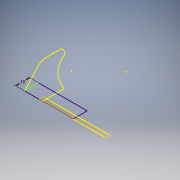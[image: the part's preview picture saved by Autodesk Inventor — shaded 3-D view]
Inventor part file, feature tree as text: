
AUTODESK INVENTOR PART (.ipt)
format: ipt  version: 2016 (Build 200138000, 138)  size: 86,016 bytes
history: native  units: mm
features: reference x3, plane x1, sketch x1
ambient origin geometry x8: Origin, YZ Plane, XZ Plane, XY Plane, X Axis, Y Axis, Z Axis, Center Point
feature tree (5):
  plane  "Work Plane1"
  sketch  "Sketch1"  dims[d0=10.0mm]
  reference  "Reference1"
  reference  "Reference2"
  reference  "Reference3"
